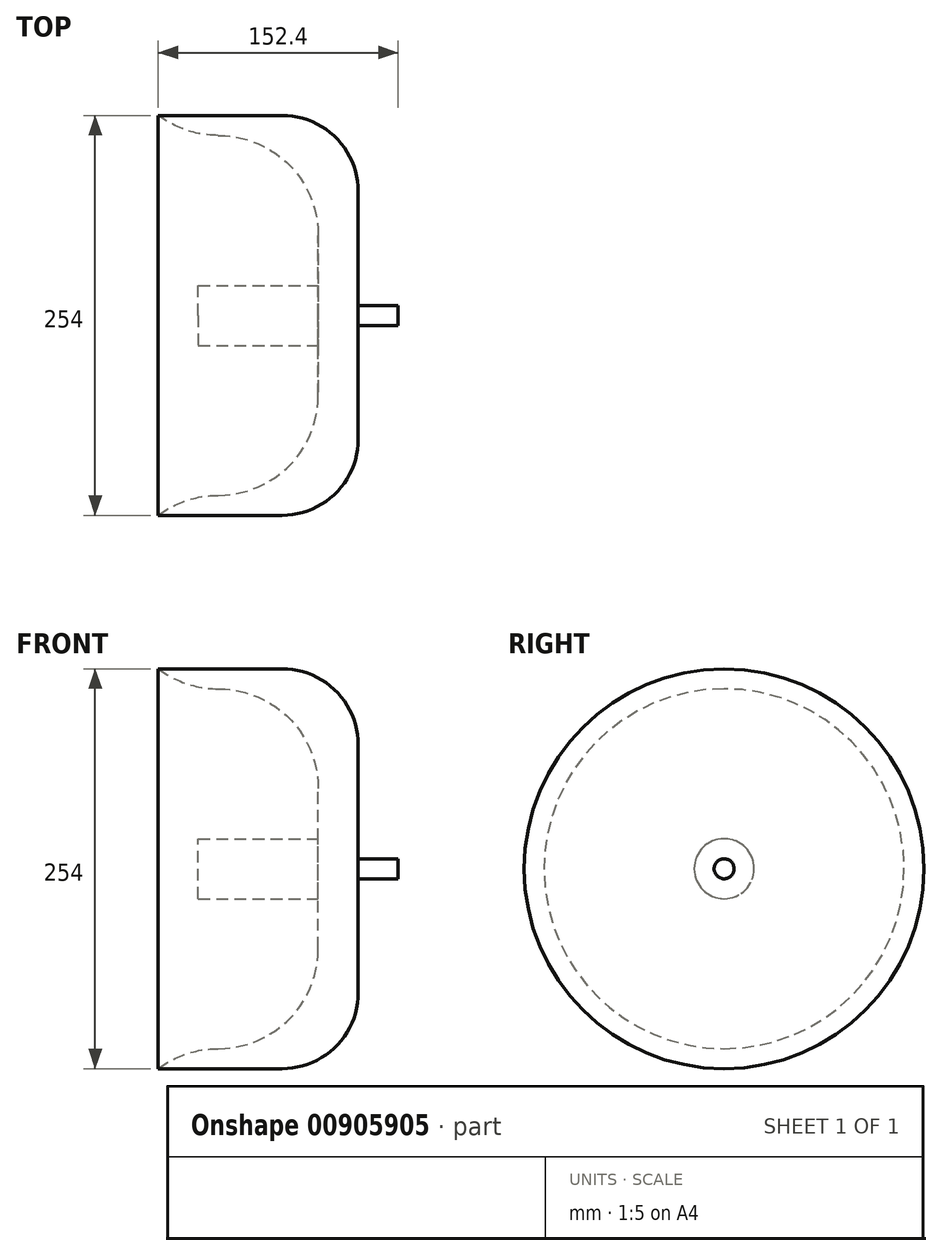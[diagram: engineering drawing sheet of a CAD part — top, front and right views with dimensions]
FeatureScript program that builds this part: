
annotation { "Feature Type Name" : "Feature", "Feature Type Description" : "" }
export const myFeature = defineFeature(function(context is Context, id is Id, definition is map)
    precondition{}
    {
        {
            var Q0;
            Q0=qCreatedBy(makeId("Right.planeOp"),FACE);
            var sketch = newSketch(context, id + "F0", { "sketchPlane" : qUnion([Q0])});
            skCircle(sketch, "E0", {"center": v(0, 0) * mm, "radius": 127 * mm});
            skSolve(sketch);
        }
        {
            var Q0;
            Q0=makeQuery(id+"F0.imprint","IMPRINT",FACE,{"disambiguationData":[TD([[makeQuery(id+"F0.imprint","IMPRINT",EDGE,{"derivedFrom":sQuery(id+"F0.wireOp",EDGE,"E0")}),1.0]])]});
            extrude(context, id + "F1", {"entities" : qUnion([Q0]), "surfaceOperationType" : NewSurfaceOperationType.ADD, "depth" : 127 * mm, "offsetDistance" : 25.4 * mm});
        }
        {
            var Q0;
            Q0=qCreatedBy(makeId("Right.planeOp"),FACE);
            var sketch = newSketch(context, id + "F2", { "sketchPlane" : qUnion([Q0])});
            skCircle(sketch, "E1", {"center": v(0, 0) * mm, "radius": 114.3 * mm});
            skSolve(sketch);
        }
        {
            var Q0;
            Q0 = qSketchRegion(id + "F2", true);
            extrude(context, id + "F3", {"entities" : qUnion([Q0]), "operationType" : NewBodyOperationType.REMOVE, "depth" : 101.6 * mm, "offsetDistance" : 25.4 * mm});
        }
        {
            var Q0;
            Q0=makeQuery(id+"F1.opExtrude","CAP_EDGE",EDGE,{"disambiguationData":[OSD([sQuery(id+"F0.wireOp",EDGE,"E0")])],"isStart":false});
            fillet(context, id + "F4", {"entities" : qUnion([Q0]), "radius" : 48.26 * mm, "tangentPropagation" : true, "allowEdgeOverflow" : false});
        }
        {
            var Q0;
            Q0=makeQuery(id+"F3.boolean.opBoolean","COPY",FACE,{"derivedFrom":makeQuery(id+"F3.opExtrude","SWEPT_FACE",FACE,{"disambiguationData":[OSD([sQuery(id+"F2.wireOp",EDGE,"E1")])]})});
            fillet(context, id + "F5", {"entities" : qUnion([Q0]), "radius" : 63.5 * mm, "tangentPropagation" : true, "allowEdgeOverflow" : false});
        }
        {
            var Q0;
            Q0=makeQuery(id+"F1.opExtrude","CAP_FACE",FACE,{"disambiguationData":[OSD([sQuery(id+"F0.wireOp",EDGE,"E0")])],"isStart":false});
            var sketch = newSketch(context, id + "F6", { "sketchPlane" : qUnion([Q0])});
            skCircle(sketch, "E2", {"center": v(0, 0) * mm, "radius": 6.35 * mm});
            skSolve(sketch);
        }
        {
            var Q0;
            Q0=makeQuery(id+"F6.imprint","IMPRINT",FACE,{"disambiguationData":[TD([[makeQuery(id+"F6.imprint","IMPRINT",EDGE,{"derivedFrom":sQuery(id+"F6.wireOp",EDGE,"E2")}),1.0]])]});
            extrude(context, id + "F7", {"entities" : qUnion([Q0]), "operationType" : NewBodyOperationType.ADD, "depth" : 25.4 * mm, "offsetDistance" : 25.4 * mm});
        }
        {
            var Q0;
            Q0=makeQuery(id+"F3.boolean.opBoolean","COPY",FACE,{"derivedFrom":makeQuery(id+"F3.opExtrude","CAP_FACE",FACE,{"disambiguationData":[OSD([sQuery(id+"F2.wireOp",EDGE,"E1")])],"isStart":false})});
            var sketch = newSketch(context, id + "F8", { "sketchPlane" : qUnion([Q0])});
            skCircle(sketch, "E3", {"center": v(0, 0) * mm, "radius": 19.05 * mm});
            skSolve(sketch);
        }
        {
            var Q0;
            Q0=makeQuery(id+"F8.imprint","IMPRINT",FACE,{"disambiguationData":[TD([[makeQuery(id+"F8.imprint","IMPRINT",EDGE,{"derivedFrom":sQuery(id+"F8.wireOp",EDGE,"E3")}),1.0]])]});
            extrude(context, id + "F9", {"entities" : qUnion([Q0]), "operationType" : NewBodyOperationType.ADD, "depth" : 76.2 * mm, "offsetDistance" : 25.4 * mm});
        }
    });
